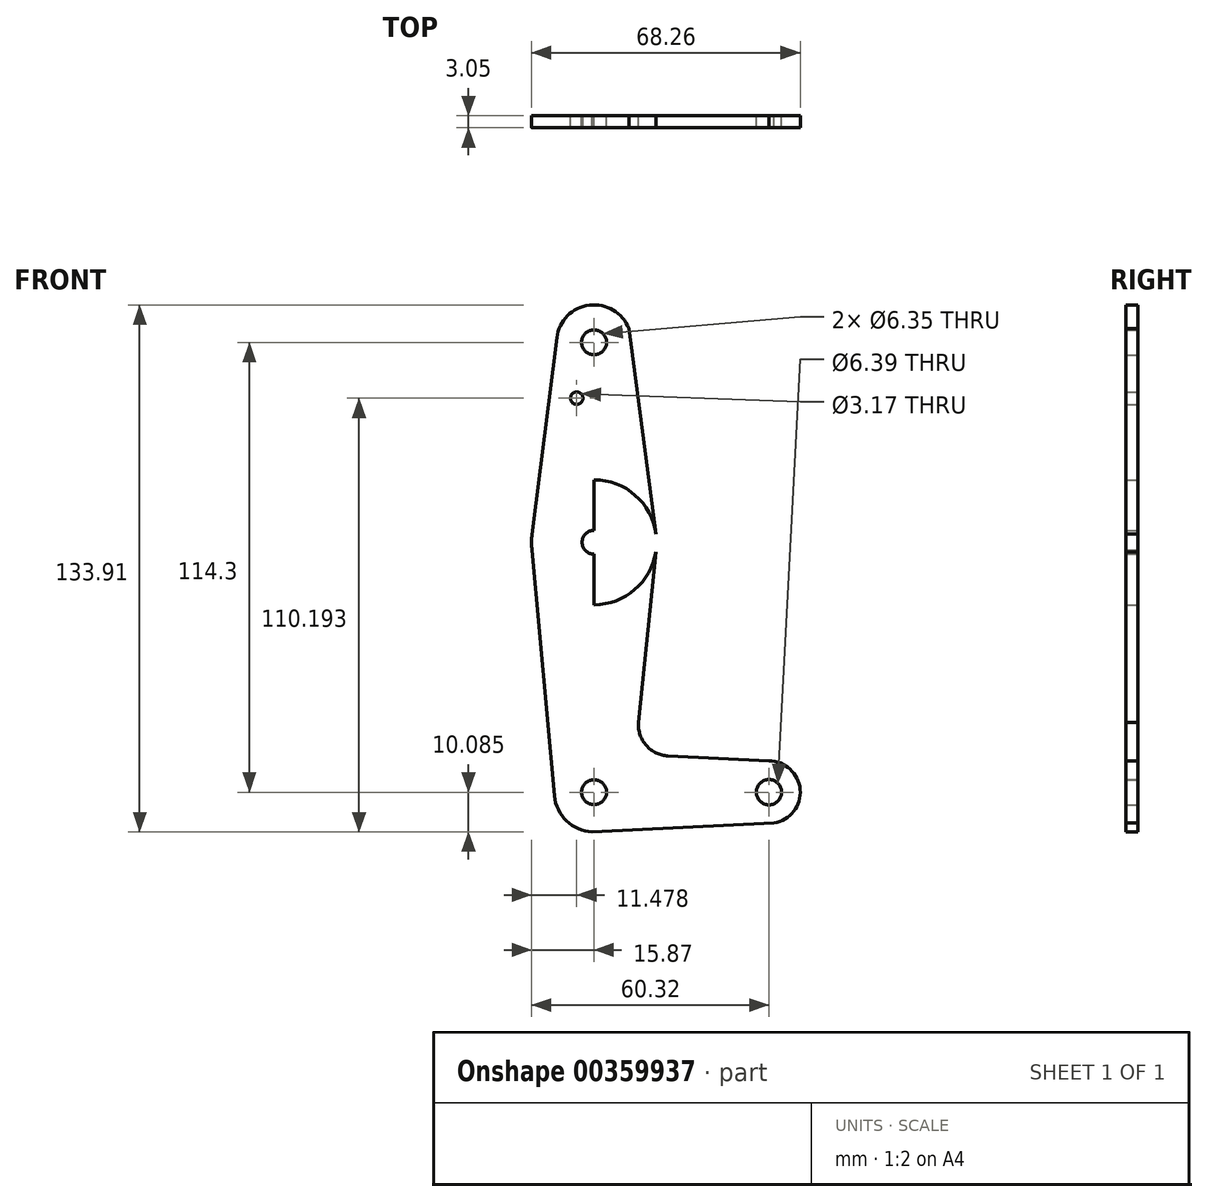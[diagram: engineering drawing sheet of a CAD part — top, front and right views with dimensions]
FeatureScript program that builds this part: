
annotation { "Feature Type Name" : "Feature", "Feature Type Description" : "" }
export const myFeature = defineFeature(function(context is Context, id is Id, definition is map)
    precondition{}
    {
        {
            var Q0;
            Q0=qCreatedBy(makeId("Front.planeOp"),FACE);
            var sketch = newSketch(context, id + "F0", { "sketchPlane" : qUnion([Q0])});
            skLineSegment(sketch, "E0", {"start": v(-44.45, 56.92) * mm, "end": v(-44.45, -57.38) * mm});
            skLineSegment(sketch, "E1", {"start": v(-44.45, -57.38) * mm, "end": v(0, -57.38) * mm});
            skCircle(sketch, "E2", {"center": v(-44.45, 56.92) * mm, "radius": 3.18 * mm});
            skCircle(sketch, "E3", {"center": v(-44.45, 56.92) * mm, "radius": 9.53 * mm});
            skCircle(sketch, "E4", {"center": v(-44.45, 6.12) * mm, "radius": 3.04 * mm});
            skCircle(sketch, "E5", {"center": v(-44.45, 6.12) * mm, "radius": 15.88 * mm});
            skCircle(sketch, "E6", {"center": v(-44.45, -57.38) * mm, "radius": 3.18 * mm});
            skCircle(sketch, "E7", {"center": v(-44.45, -57.38) * mm, "radius": 10.1 * mm});
            skCircle(sketch, "E8", {"center": v(0, -57.38) * mm, "radius": 3.2 * mm});
            skCircle(sketch, "E9", {"center": v(0, -57.38) * mm, "radius": 7.94 * mm});
            skCircle(sketch, "E10", {"center": v(-48.84, 42.73) * mm, "radius": 1.59 * mm});
            skLineSegment(sketch, "E11", {"start": v(-35.59, 60.42) * mm, "end": v(-28.45, 6.2) * mm});
            skLineSegment(sketch, "E12", {"start": v(-53.9, 58.1) * mm, "end": v(-60.2, 8.1) * mm});
            skLineSegment(sketch, "E13", {"start": v(-60.2, 8.1) * mm, "end": v(-60.2, 4.14) * mm});
            skLineSegment(sketch, "E14", {"start": v(-60.2, 4.14) * mm, "end": v(-54.5, -58.3) * mm});
            skLineSegment(sketch, "E15", {"start": v(0, -49.44) * mm, "end": v(-25.6, -48.19) * mm});
            skArc(sketch, "E16.filletArc", {"start": v(-33.15, -39.7) * mm, "mid": v(-31.16, -45.53) * mm, "end": v(-25.6, -48.19) * mm});
            skPoint(sketch, "E17.end.orphan", {"position": v(0, -65.32) * mm});
            skLineSegment(sketch, "E18", {"start": v(-44.95, -67.46) * mm, "end": v(1.32, -65.2) * mm});
            skLineSegment(sketch, "E19", {"start": v(-28.76, 3.71) * mm, "end": v(-33.15, -39.7) * mm});
            skSolve(sketch);
        }
        {
            var Q0;
            {var subQ0=sQuery(id+"F0.wireOp",EDGE,"E11");var subQ1=sQuery(id+"F0.wireOp",EDGE,"E3");var subQ2=makeQuery(id+"F0.imprint","INTERSECT",VERTEX,{"disambiguationData":[OD(0.0)],"derivedFrom":[subQ1,subQ0]});Q0=makeQuery(id+"F0.imprint","IMPRINT",FACE,{"disambiguationData":[TD([[makeQuery(id+"F0.imprint","IMPRINT",EDGE,{"disambiguationData":[TD([[subQ2,1.0]])],"derivedFrom":subQ1}),1.0]])]});}
            var Q1;
            {var subQ0=sQuery(id+"F0.wireOp",EDGE,"E13");Q1=makeQuery(id+"F0.imprint","IMPRINT",FACE,{"disambiguationData":[TD([[makeQuery(id+"F0.imprint","IMPRINT",EDGE,{"derivedFrom":subQ0}),-1.0]])]});}
            var Q2;
            {var subQ0=sQuery(id+"F0.wireOp",EDGE,"SUE6N16U-VqjM-IYjU-v398-A2tttwida5cV");var subQ1=sQuery(id+"F0.wireOp",EDGE,"E7");var subQ2=makeQuery(id+"F0.imprint","INTERSECT",VERTEX,{"disambiguationData":[OD(0.0)],"derivedFrom":[subQ1,subQ0]});Q2=makeQuery(id+"F0.imprint","IMPRINT",FACE,{"disambiguationData":[TD([[makeQuery(id+"F0.imprint","IMPRINT",EDGE,{"disambiguationData":[TD([[subQ2,-1.0]])],"derivedFrom":subQ1}),1.0]])]});}
            var Q3;
            {var subQ0=sQuery(id+"F0.wireOp",EDGE,"E3");var subQ1=sQuery(id+"F0.wireOp",EDGE,"E0");var subQ2=makeQuery(id+"F0.imprint","INTERSECT",VERTEX,{"derivedFrom":[subQ1,subQ0]});Q3=makeQuery(id+"F0.imprint","IMPRINT",FACE,{"disambiguationData":[TD([[makeQuery(id+"F0.imprint","IMPRINT",EDGE,{"disambiguationData":[TD([[subQ2,-1.0]])],"derivedFrom":subQ1}),1.0]])]});}
            var Q4;
            {var subQ5=sQuery(id+"F0.wireOp",EDGE,"E14");Q4=makeQuery(id+"F0.imprint","IMPRINT",FACE,{"disambiguationData":[TD([[makeQuery(id+"F0.imprint","IMPRINT",EDGE,{"derivedFrom":subQ5}),1.0]])]});}
            var Q5;
            {var subQ0=sQuery(id+"F0.wireOp",EDGE,"E7");var subQ1=sQuery(id+"F0.wireOp",EDGE,"E0");var subQ2=makeQuery(id+"F0.imprint","INTERSECT",VERTEX,{"derivedFrom":[subQ1,subQ0]});Q5=makeQuery(id+"F0.imprint","IMPRINT",FACE,{"disambiguationData":[TD([[makeQuery(id+"F0.imprint","IMPRINT",EDGE,{"disambiguationData":[TD([[subQ2,-1.0]])],"derivedFrom":subQ1}),1.0]])]});}
            var Q6;
            Q6=makeQuery(id+"F0.imprint","IMPRINT",FACE,{"disambiguationData":[TD([[makeQuery(id+"F0.imprint","IMPRINT",EDGE,{"derivedFrom":sQuery(id+"F0.wireOp",EDGE,"E10")}),-1.0]])]});
            var Q7;
            {var subQ0=sQuery(id+"F0.wireOp",EDGE,"E5");var subQ2=sQuery(id+"F0.wireOp",EDGE,"E0");var subQ3=makeQuery(id+"F0.imprint","INTERSECT",VERTEX,{"disambiguationData":[OD(0.0)],"derivedFrom":[subQ2,subQ0]});Q7=makeQuery(id+"F0.imprint","IMPRINT",FACE,{"disambiguationData":[TD([[makeQuery(id+"F0.imprint","IMPRINT",EDGE,{"disambiguationData":[TD([[subQ3,-1.0]])],"derivedFrom":subQ2}),1.0]])]});}
            var Q8;
            {var subQ5=sQuery(id+"F0.wireOp",EDGE,"37y9YS2i-nUgY-rdlT-YMJj-plCXzkCF4wUm");Q8=makeQuery(id+"F0.imprint","IMPRINT",FACE,{"disambiguationData":[TD([[makeQuery(id+"F0.imprint","IMPRINT",EDGE,{"derivedFrom":subQ5}),-1.0]])]});}
            var Q9;
            Q9=makeQuery(id+"F0.imprint","IMPRINT",FACE,{"disambiguationData":[TD([[makeQuery(id+"F0.imprint","IMPRINT",EDGE,{"derivedFrom":sQuery(id+"F0.wireOp",EDGE,"E2")}),-1.0]])]});
            var Q10;
            {var subQ4=sQuery(id+"F0.wireOp",EDGE,"E13");Q10=makeQuery(id+"F0.imprint","IMPRINT",FACE,{"disambiguationData":[TD([[makeQuery(id+"F0.imprint","IMPRINT",EDGE,{"derivedFrom":subQ4}),1.0]])]});}
            var Q11;
            {var subQ0=sQuery(id+"F0.wireOp",EDGE,"E9");var subQ1=sQuery(id+"F0.wireOp",EDGE,"E1");var subQ2=makeQuery(id+"F0.imprint","INTERSECT",VERTEX,{"derivedFrom":[subQ1,subQ0]});Q11=makeQuery(id+"F0.imprint","IMPRINT",FACE,{"disambiguationData":[TD([[makeQuery(id+"F0.imprint","IMPRINT",EDGE,{"disambiguationData":[TD([[subQ2,1.0]])],"derivedFrom":subQ1}),-1.0]])]});}
            var Q12;
            {var subQ10=sQuery(id+"F0.wireOp",EDGE,"E15");Q12=makeQuery(id+"F0.imprint","IMPRINT",FACE,{"disambiguationData":[TD([[makeQuery(id+"F0.imprint","IMPRINT",EDGE,{"derivedFrom":subQ10}),1.0]])]});}
            var Q13;
            {var subQ0=sQuery(id+"F0.wireOp",EDGE,"E7");var subQ2=sQuery(id+"F0.wireOp",EDGE,"E0");var subQ3=makeQuery(id+"F0.imprint","INTERSECT",VERTEX,{"derivedFrom":[subQ2,subQ0]});Q13=makeQuery(id+"F0.imprint","IMPRINT",FACE,{"disambiguationData":[TD([[makeQuery(id+"F0.imprint","IMPRINT",EDGE,{"disambiguationData":[TD([[subQ3,-1.0]])],"derivedFrom":subQ2}),-1.0]])]});}
            var Q14;
            Q14=makeQuery(id+"F0.imprint","IMPRINT",FACE,{"disambiguationData":[TD([[makeQuery(id+"F0.imprint","IMPRINT",EDGE,{"derivedFrom":sQuery(id+"F0.wireOp",EDGE,"E8")}),-1.0]])]});
            extrude(context, id + "F1", {"entities" : qUnion([Q0, Q1, Q2, Q3, Q4, Q5, Q6, Q7, Q8, Q9, Q10, Q11, Q12, Q13, Q14]), "depth" : 3.05 * mm});
        }
    });
